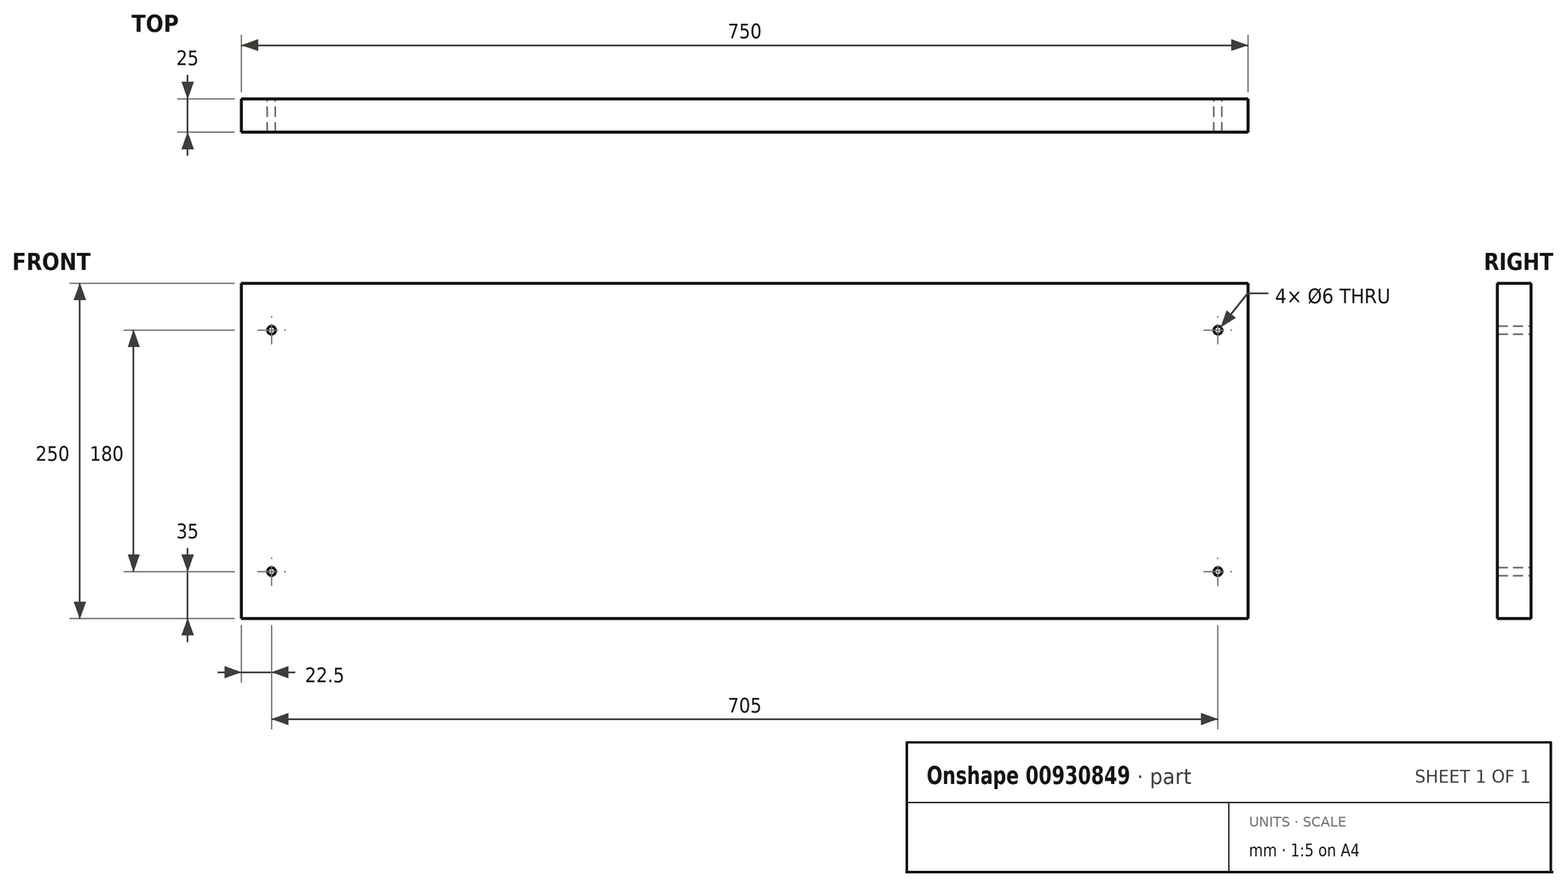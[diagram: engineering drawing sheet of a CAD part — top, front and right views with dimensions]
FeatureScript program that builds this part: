
annotation { "Feature Type Name" : "Feature", "Feature Type Description" : "" }
export const myFeature = defineFeature(function(context is Context, id is Id, definition is map)
    precondition{}
    {
        {
            var Q0;
            Q0=qCreatedBy(makeId("Front.planeOp"),FACE);
            var sketch = newSketch(context, id + "F0", { "sketchPlane" : qUnion([Q0])});
            skLineSegment(sketch, "E0.bottom", {"start": v(352.5, 90) * mm, "end": v(-352.5, 90) * mm, "construction": true});
            skLineSegment(sketch, "E0.top", {"start": v(352.5, -90) * mm, "end": v(-352.5, -90) * mm, "construction": true});
            skLineSegment(sketch, "E0.left", {"start": v(352.5, 90) * mm, "end": v(352.5, -90) * mm, "construction": true});
            skLineSegment(sketch, "E0.right", {"start": v(-352.5, 90) * mm, "end": v(-352.5, -90) * mm, "construction": true});
            skPoint(sketch, "E0.middle", {"position": v(0, 0) * mm});
            skCircle(sketch, "E1", {"center": v(-352.5, 90) * mm, "radius": 3 * mm});
            skCircle(sketch, "E2", {"center": v(352.5, 90) * mm, "radius": 3 * mm});
            skCircle(sketch, "E3", {"center": v(-352.5, -90) * mm, "radius": 3 * mm});
            skCircle(sketch, "E4", {"center": v(352.5, -90) * mm, "radius": 3 * mm});
            skLineSegment(sketch, "E5.bottom", {"start": v(375, 125) * mm, "end": v(-375, 125) * mm});
            skLineSegment(sketch, "E5.top", {"start": v(375, -125) * mm, "end": v(-375, -125) * mm});
            skLineSegment(sketch, "E5.left", {"start": v(375, 125) * mm, "end": v(375, -125) * mm});
            skLineSegment(sketch, "E5.right", {"start": v(-375, 125) * mm, "end": v(-375, -125) * mm});
            skSolve(sketch);
        }
        {
            var Q0;
            Q0 = qSketchRegion(id + "F0", true);
            extrude(context, id + "F1", {"entities" : qUnion([Q0]), "depth" : 25 * mm, "offsetDistance" : 25 * mm});
        }
    });
